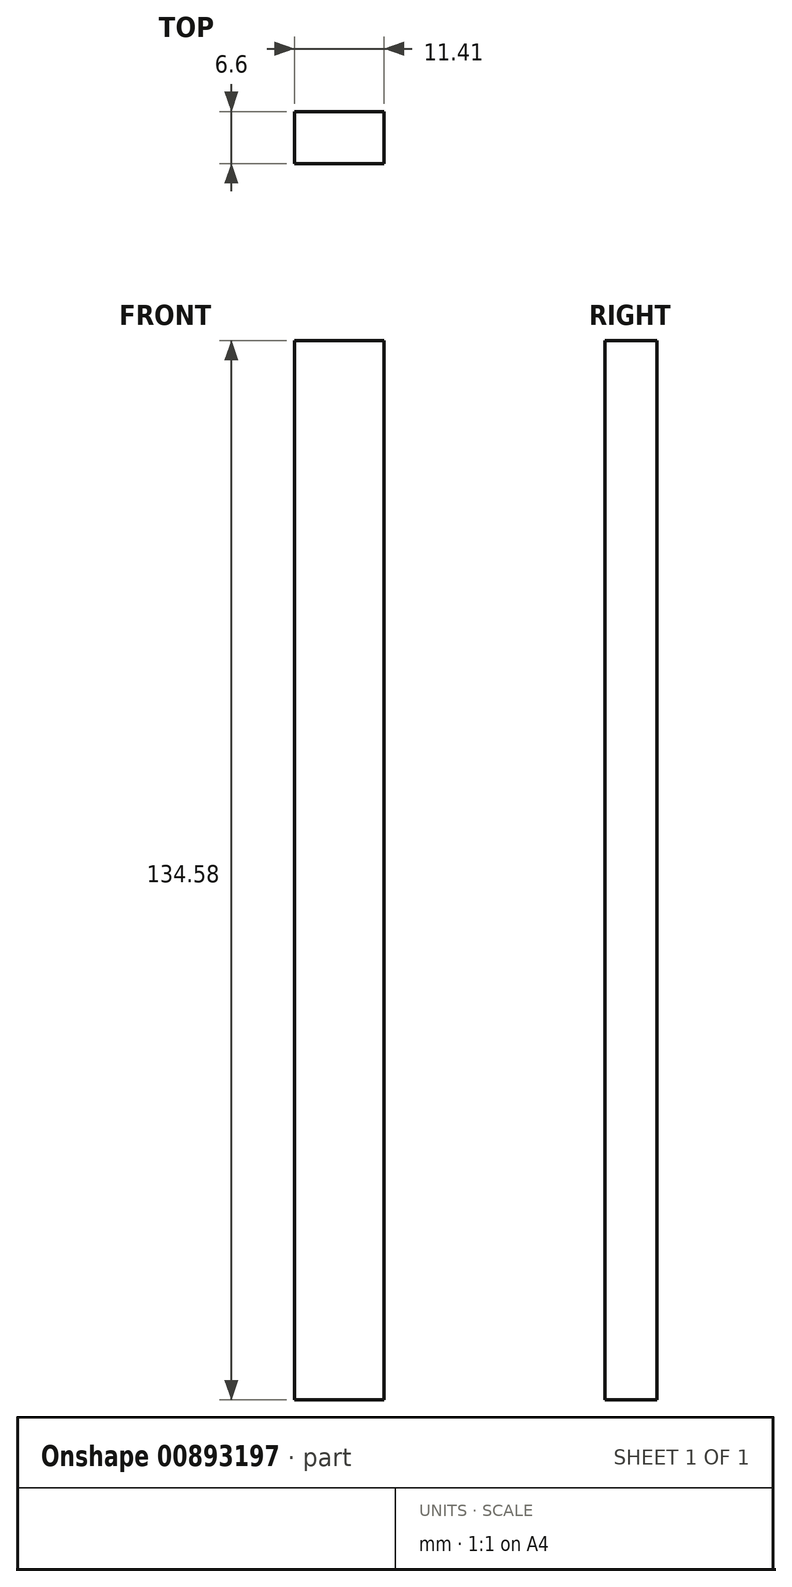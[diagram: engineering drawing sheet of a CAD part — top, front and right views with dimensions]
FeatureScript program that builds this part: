
annotation { "Feature Type Name" : "Feature", "Feature Type Description" : "" }
export const myFeature = defineFeature(function(context is Context, id is Id, definition is map)
    precondition{}
    {
        {
            var Q0;
            Q0=qCreatedBy(makeId("Front.planeOp"),FACE);
            var sketch = newSketch(context, id + "F0", { "sketchPlane" : qUnion([Q0])});
            skLineSegment(sketch, "E0.bottom", {"start": v(-54.43, -10.2) * mm, "end": v(-43.02, -10.2) * mm});
            skLineSegment(sketch, "E0.top", {"start": v(-54.43, 124.37) * mm, "end": v(-43.02, 124.37) * mm});
            skLineSegment(sketch, "E0.left", {"start": v(-54.43, -10.2) * mm, "end": v(-54.43, 124.37) * mm});
            skLineSegment(sketch, "E0.right", {"start": v(-43.02, -10.2) * mm, "end": v(-43.02, 124.37) * mm});
            skSolve(sketch);
        }
        {
            var Q0;
            Q0 = qSketchRegion(id + "F0", true);
            extrude(context, id + "F1", {"entities" : qUnion([Q0]), "depth" : 6.6 * mm, "offsetDistance" : 25.4 * mm});
        }
    });
